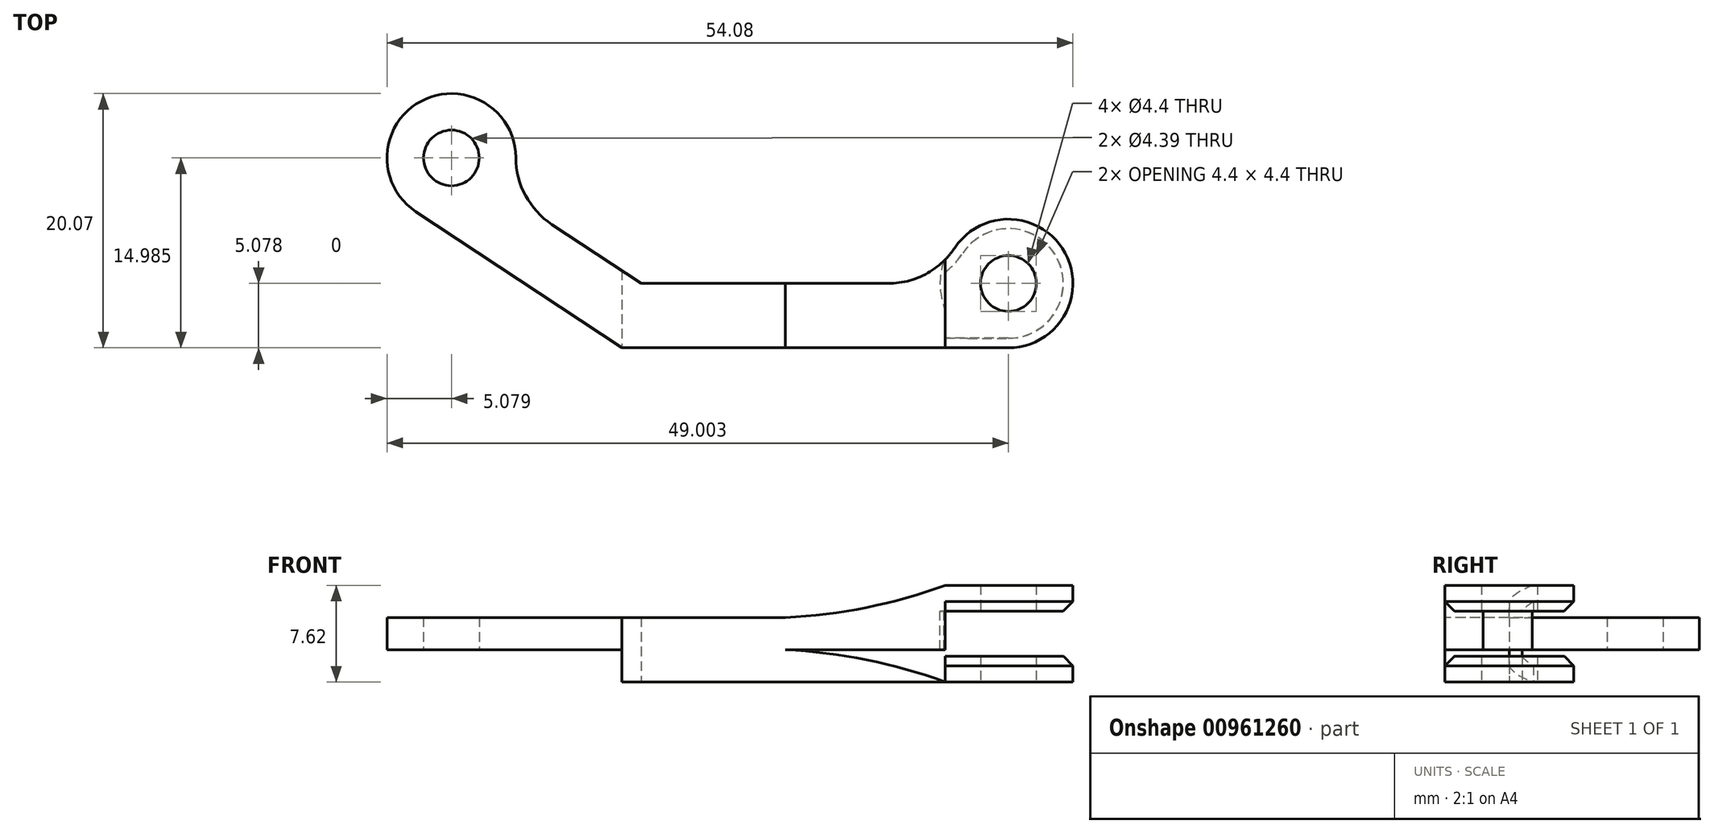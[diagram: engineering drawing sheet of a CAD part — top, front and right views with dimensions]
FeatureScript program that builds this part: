
annotation { "Feature Type Name" : "Feature", "Feature Type Description" : "" }
export const myFeature = defineFeature(function(context is Context, id is Id, definition is map)
    precondition{}
    {
        {
            var Q0;
            Q0=qCreatedBy(makeId("Top.planeOp"),FACE);
            var sketch = newSketch(context, id + "F0", { "sketchPlane" : qUnion([Q0])});
            skLineSegment(sketch, "E0.bottom", {"start": v(46.3, -27.78) * mm, "end": v(15.82, -27.78) * mm});
            skLineSegment(sketch, "E0.top", {"start": v(36.8, -22.7) * mm, "end": v(17.35, -22.7) * mm});
            skArc(sketch, "E1", {"start": v(46.3, -27.78) * mm, "mid": v(50.78, -20.3) * mm, "end": v(42.08, -19.88) * mm});
            skLineSegment(sketch, "E2", {"start": v(46.3, -27.78) * mm, "end": v(46.3, -34.93) * mm, "construction": true});
            skPoint(sketch, "E3.visualSharp", {"position": v(41.22, -22.7) * mm});
            skArc(sketch, "E3.filletArc", {"start": v(36.8, -22.7) * mm, "mid": v(39.8, -21.95) * mm, "end": v(42.08, -19.88) * mm});
            skPoint(sketch, "E4.visualSharp", {"position": v(1.41, -27.78) * mm});
            skCircle(sketch, "E5", {"center": v(46.3, -22.7) * mm, "radius": 2.2 * mm});
            skPoint(sketch, "E6.visualSharp", {"position": v(1.41, -22.7) * mm});
            skLineSegment(sketch, "E7", {"start": v(17.35, -22.7) * mm, "end": v(10.3, -18.04) * mm});
            skLineSegment(sketch, "E8", {"start": v(-0.42, -17.03) * mm, "end": v(15.82, -27.78) * mm});
            skArc(sketch, "E9", {"start": v(7.46, -12.77) * mm, "mid": v(-0.04, -8.33) * mm, "end": v(-0.42, -17.03) * mm});
            skCircle(sketch, "E10", {"center": v(2.38, -12.8) * mm, "radius": 2.2 * mm});
            skPoint(sketch, "E11.end.orphan", {"position": v(-3.67, -27.78) * mm});
            skPoint(sketch, "E12.visualSharp", {"position": v(6.62, -15.6) * mm});
            skArc(sketch, "E12.filletArc", {"start": v(7.46, -12.77) * mm, "mid": v(8.22, -15.76) * mm, "end": v(10.3, -18.04) * mm});
            skSolve(sketch);
        }
        {
            var Q0;
            Q0=makeQuery(id+"F0.imprint","IMPRINT",FACE,{"disambiguationData":[TD([[makeQuery(id+"F0.imprint","IMPRINT",EDGE,{"derivedFrom":sQuery(id+"F0.wireOp",EDGE,"E0.bottom")}),-1.0]])]});
            extrude(context, id + "F1", {"entities" : qUnion([Q0]), "depth" : 7.62 * mm, "offsetDistance" : 25.4 * mm});
        }
        {
            var Q0;
            Q0=makeQuery(id+"F1.opExtrude","SWEPT_FACE",FACE,{"disambiguationData":[OSD([sQuery(id+"F0.wireOp",EDGE,"E0.bottom")])]});
            var sketch = newSketch(context, id + "F2", { "sketchPlane" : qUnion([Q0])});
            skLineSegment(sketch, "E13.bottom", {"start": v(41.32, 7.62) * mm, "end": v(-12.19, 7.62) * mm});
            skLineSegment(sketch, "E13.top", {"start": v(41.32, 0) * mm, "end": v(-12.19, 0) * mm});
            skLineSegment(sketch, "E13.left", {"start": v(41.32, 7.62) * mm, "end": v(41.32, 0) * mm});
            skLineSegment(sketch, "E13.right", {"start": v(-12.19, 7.62) * mm, "end": v(-12.19, 0) * mm});
            skLineSegment(sketch, "E14.bottom", {"start": v(41.32, 5.08) * mm, "end": v(-12.19, 5.08) * mm});
            skLineSegment(sketch, "E14.top", {"start": v(41.32, 2.54) * mm, "end": v(-12.19, 2.54) * mm});
            skLineSegment(sketch, "E14.left", {"start": v(41.32, 5.08) * mm, "end": v(41.32, 2.54) * mm});
            skLineSegment(sketch, "E14.right", {"start": v(-12.19, 5.08) * mm, "end": v(-12.19, 2.54) * mm});
            skLineSegment(sketch, "E15", {"start": v(41.32, 5.08) * mm, "end": v(68.97, 5.08) * mm});
            skLineSegment(sketch, "E16", {"start": v(68.97, 5.08) * mm, "end": v(68.97, 2.54) * mm});
            skLineSegment(sketch, "E17", {"start": v(68.97, 2.54) * mm, "end": v(41.32, 2.54) * mm});
            skLineSegment(sketch, "E18.bottom", {"start": v(41.32, 5.08) * mm, "end": v(71.35, 5.08) * mm});
            skLineSegment(sketch, "E18.top", {"start": v(41.32, 11) * mm, "end": v(71.35, 11) * mm});
            skLineSegment(sketch, "E18.left", {"start": v(41.32, 5.08) * mm, "end": v(41.32, 11) * mm});
            skLineSegment(sketch, "E18.right", {"start": v(71.35, 5.08) * mm, "end": v(71.35, 11) * mm});
            skLineSegment(sketch, "E19.bottom", {"start": v(41.32, 2.54) * mm, "end": v(71.71, 2.54) * mm});
            skLineSegment(sketch, "E19.top", {"start": v(41.32, -4.78) * mm, "end": v(71.71, -4.78) * mm});
            skLineSegment(sketch, "E19.left", {"start": v(41.32, 2.54) * mm, "end": v(41.32, -4.78) * mm});
            skLineSegment(sketch, "E19.right", {"start": v(71.71, 2.54) * mm, "end": v(71.71, -4.78) * mm});
            skLineSegment(sketch, "E20", {"start": v(43.25, 3.81) * mm, "end": v(41.32, 3.81) * mm, "construction": true});
            skArc(sketch, "E21", {"start": v(28.72, 5.08) * mm, "mid": v(35.12, 5.88) * mm, "end": v(41.32, 7.62) * mm});
            skArc(sketch, "E22.MirrorCS", {"start": v(28.72, 2.54) * mm, "mid": v(35.12, 1.74) * mm, "end": v(41.32, 0) * mm});
            skLineSegment(sketch, "E23", {"start": v(41.32, 5.58) * mm, "end": v(71.35, 5.58) * mm});
            skLineSegment(sketch, "E24", {"start": v(41.32, 2.04) * mm, "end": v(71.71, 2.04) * mm});
            skSolve(sketch);
        }
        {
            var Q0;
            {var subQ0=sQuery(id+"F2.wireOp",EDGE,"E13.bottom");var subQ3=sQuery(id+"F2.wireOp",EDGE,"E13.right");var subQ4=makeQuery(id+"F2.imprint","INTERSECT",VERTEX,{"derivedFrom":[subQ0,subQ3]});Q0=makeQuery(id+"F2.imprint","IMPRINT",FACE,{"disambiguationData":[TD([[makeQuery(id+"F2.imprint","IMPRINT",EDGE,{"disambiguationData":[TD([[subQ4,-1.0]])],"derivedFrom":subQ3}),1.0]])]});}
            var Q1;
            {var subQ4=sQuery(id+"F2.wireOp",EDGE,"E21");Q1=makeQuery(id+"F2.imprint","IMPRINT",FACE,{"disambiguationData":[TD([[makeQuery(id+"F2.imprint","IMPRINT",EDGE,{"derivedFrom":subQ4}),1.0]])]});}
            var Q2;
            {var subQ0=sQuery(id+"F2.wireOp",EDGE,"E13.top");var subQ3=sQuery(id+"F2.wireOp",EDGE,"E13.right");var subQ4=makeQuery(id+"F2.imprint","INTERSECT",VERTEX,{"derivedFrom":[subQ0,subQ3]});Q2=makeQuery(id+"F2.imprint","IMPRINT",FACE,{"disambiguationData":[TD([[makeQuery(id+"F2.imprint","IMPRINT",EDGE,{"disambiguationData":[TD([[subQ4,1.0]])],"derivedFrom":subQ3}),1.0]])]});}
            var Q3;
            {var subQ4=sQuery(id+"F2.wireOp",EDGE,"E22.MirrorCS");Q3=makeQuery(id+"F2.imprint","IMPRINT",FACE,{"disambiguationData":[TD([[makeQuery(id+"F2.imprint","IMPRINT",EDGE,{"derivedFrom":subQ4}),-1.0]])]});}
            var Q4;
            {var subQ0=sQuery(id+"F2.wireOp",EDGE,"E16");Q4=makeQuery(id+"F2.imprint","IMPRINT",FACE,{"disambiguationData":[TD([[makeQuery(id+"F2.imprint","IMPRINT",EDGE,{"derivedFrom":subQ0}),-1.0]])]});}
            var Q5;
            {var subQ0=sQuery(id+"F2.wireOp",EDGE,"E15");var subQ1=sQuery(id+"F2.wireOp",EDGE,"E13.left");var subQ2=makeQuery(id+"F2.imprint","INTERSECT",VERTEX,{"derivedFrom":[subQ1,sQuery(id+"F2.wireOp",EDGE,"E14.bottom"),subQ0]});Q5=makeQuery(id+"F2.imprint","IMPRINT",FACE,{"disambiguationData":[TD([[makeQuery(id+"F2.imprint","IMPRINT",EDGE,{"disambiguationData":[TD([[subQ2,-1.0]])],"derivedFrom":subQ1}),1.0]])]});}
            var Q6;
            {var subQ1=sQuery(id+"F2.wireOp",EDGE,"E13.left");var subQ3=sQuery(id+"F2.wireOp",EDGE,"E23");var subQ4=makeQuery(id+"F2.imprint","INTERSECT",VERTEX,{"derivedFrom":[subQ1,subQ3]});Q6=makeQuery(id+"F2.imprint","IMPRINT",FACE,{"disambiguationData":[TD([[makeQuery(id+"F2.imprint","IMPRINT",EDGE,{"disambiguationData":[TD([[subQ4,-1.0]])],"derivedFrom":subQ1}),1.0]])]});}
            var Q7;
            {var subQ7=sQuery(id+"F2.wireOp",EDGE,"E18.bottom");Q7=makeQuery(id+"F2.imprint","IMPRINT",FACE,{"disambiguationData":[TD([[makeQuery(id+"F2.imprint","IMPRINT",EDGE,{"derivedFrom":subQ7}),1.0]])]});}
            var Q8;
            {var subQ0=sQuery(id+"F2.wireOp",EDGE,"E24");var subQ1=sQuery(id+"F2.wireOp",EDGE,"E13.left");var subQ2=makeQuery(id+"F2.imprint","INTERSECT",VERTEX,{"derivedFrom":[subQ1,subQ0]});Q8=makeQuery(id+"F2.imprint","IMPRINT",FACE,{"disambiguationData":[TD([[makeQuery(id+"F2.imprint","IMPRINT",EDGE,{"disambiguationData":[TD([[subQ2,1.0]])],"derivedFrom":subQ1}),1.0]])]});}
            var Q9;
            {var subQ1=sQuery(id+"F2.wireOp",EDGE,"E19.bottom");Q9=makeQuery(id+"F2.imprint","IMPRINT",FACE,{"disambiguationData":[TD([[makeQuery(id+"F2.imprint","IMPRINT",EDGE,{"derivedFrom":subQ1}),-1.0]])]});}
            extrude(context, id + "F3", {"entities" : qUnion([Q0, Q1, Q2, Q3, Q4, Q5, Q6, Q7, Q8, Q9]), "operationType" : NewBodyOperationType.REMOVE, "endBound" : BoundingType.THROUGH_ALL, "oppositeDirection" : true, "depth" : 25.4 * mm, "offsetDistance" : 25.4 * mm});
        }
        {
            var Q0;
            {var subQ0=makeQuery(id+"F1.opExtrude","SWEPT_FACE",FACE,{"disambiguationData":[OSD([sQuery(id+"F0.wireOp",EDGE,"E1")])]});Q0=qUnion([makeQuery(id+"F3.boolean.opBoolean","INTERSECT",EDGE,{"derivedFrom":[subQ0,makeQuery(id+"F3.opExtrude","SWEPT_FACE",FACE,{"disambiguationData":[OSD([sQuery(id+"F2.wireOp",EDGE,"E23")])]})]}),makeQuery(id+"F3.boolean.opBoolean","INTERSECT",EDGE,{"derivedFrom":[subQ0,makeQuery(id+"F3.opExtrude","SWEPT_FACE",FACE,{"disambiguationData":[OSD([sQuery(id+"F2.wireOp",EDGE,"E24")])]})]})]);}
            var Q1;
            {var subQ0=makeQuery(id+"F1.opExtrude","SWEPT_FACE",FACE,{"disambiguationData":[OSD([sQuery(id+"F0.wireOp",EDGE,"E1")])]});Q1=qUnion([makeQuery(id+"F3.boolean.opBoolean","INTERSECT",EDGE,{"derivedFrom":[subQ0,makeQuery(id+"F3.opExtrude","SWEPT_FACE",FACE,{"disambiguationData":[OSD([sQuery(id+"F2.wireOp",EDGE,"E23")])]})]}),makeQuery(id+"F3.boolean.opBoolean","INTERSECT",EDGE,{"derivedFrom":[subQ0,makeQuery(id+"F3.opExtrude","SWEPT_FACE",FACE,{"disambiguationData":[OSD([sQuery(id+"F2.wireOp",EDGE,"E24")])]})]})]);}
            chamfer(context, id + "F4", {"entities" : qUnion([Q0, Q1]), "width" : 0.76 * mm, "tangentPropagation" : true});
        }
        {
            var Q0;
            Q0=makeQuery(id+"F3.boolean.opBoolean","COPY",FACE,{"derivedFrom":makeQuery(id+"F3.opExtrude","SWEPT_FACE",FACE,{"disambiguationData":[OSD([sQuery(id+"F2.wireOp",EDGE,"E23")])]})});
            var sketch = newSketch(context, id + "F5", { "sketchPlane" : qUnion([Q0])});
            skCircle(sketch, "E25", {"center": v(46.3, 22.7) * mm, "radius": 5.4 * mm});
            skSolve(sketch);
        }
        {
            var Q0;
            {var subQ0=sQuery(id+"F2.wireOp",EDGE,"E23");var subQ1=makeQuery(id+"F3.opExtrude","SWEPT_FACE",FACE,{"disambiguationData":[OSD([subQ0])]});var subQ2=makeQuery(id+"F3.boolean.opBoolean","COPY",FACE,{"derivedFrom":subQ1});var subQ4=makeQuery(id+"F4.opChamfer","BLEND_EDGE",EDGE,{"blendedFrom":[makeQuery(id+"F3.boolean.opBoolean","INTERSECT",EDGE,{"derivedFrom":[makeQuery(id+"F1.opExtrude","SWEPT_FACE",FACE,{"disambiguationData":[OSD([sQuery(id+"F0.wireOp",EDGE,"E3.filletArc")])]}),subQ1]}),subQ2],"blendedInto":[subQ2]});Q0=makeQuery(id+"F5.imprint","IMPRINT",FACE,{"disambiguationData":[TD([[makeQuery(id+"F5.imprint","IMPRINT",EDGE,{"derivedFrom":subQ4}),-1.0]])]});}
            extrude(context, id + "F6", {"entities" : qUnion([Q0]), "operationType" : NewBodyOperationType.REMOVE, "depth" : 3.56 * mm, "offsetDistance" : 25.4 * mm});
        }
        {
            var Q0;
            Q0=makeQuery(id+"F1.opExtrude","SWEPT_BODY",BODY,{"disambiguationData":[OSD([sQuery(id+"F0.wireOp",EDGE,"E0.bottom"),sQuery(id+"F0.wireOp",EDGE,"E0.top"),sQuery(id+"F0.wireOp",EDGE,"E1"),sQuery(id+"F0.wireOp",EDGE,"E3.filletArc"),sQuery(id+"F0.wireOp",EDGE,"E5"),sQuery(id+"F0.wireOp",EDGE,"YR7Oqlov-EFYM-y0DN-ngIu-OAyjApuZfuOU"),sQuery(id+"F0.wireOp",EDGE,"E11"),sQuery(id+"F0.wireOp",EDGE,"E6.filletArc"),sQuery(id+"F0.wireOp",EDGE,"Q6iPlcnx-GQal-Kntt-9oPM-ReCZVEJanNZy")])]});
            transform(context, id + "F7", {"entities" : qUnion([Q0]), "transformType" : TransformType.TRANSLATION_3D, "dx" : 0 * mm, "dy" : 0 * mm, "dz" : 0 * mm, "makeCopy" : true});
        }
    });
